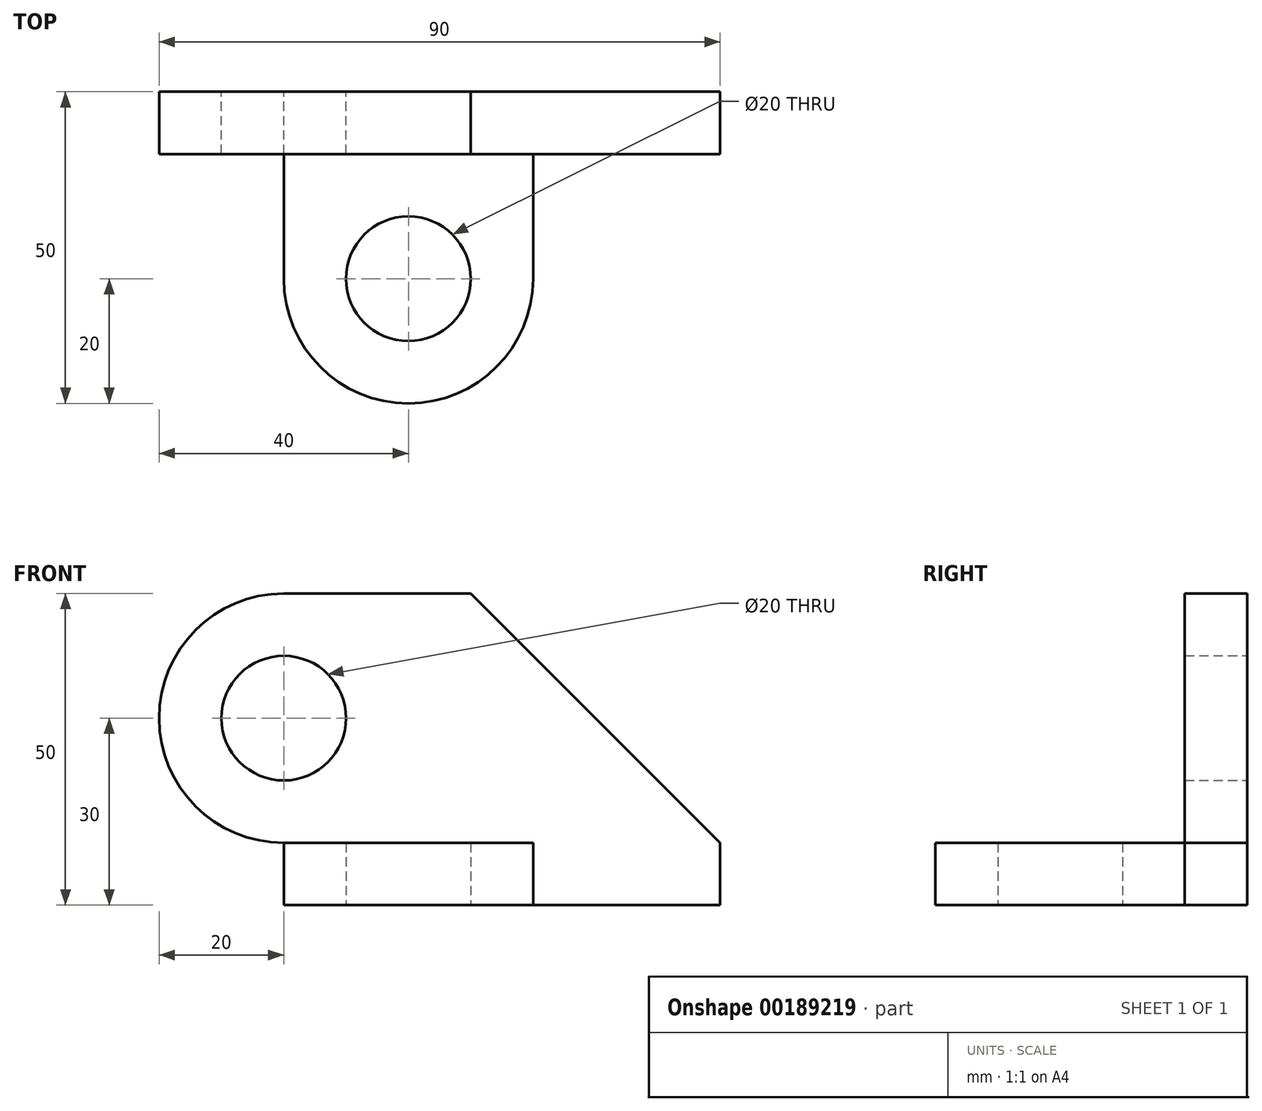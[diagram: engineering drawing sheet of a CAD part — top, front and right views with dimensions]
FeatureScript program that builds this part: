
annotation { "Feature Type Name" : "Feature", "Feature Type Description" : "" }
export const myFeature = defineFeature(function(context is Context, id is Id, definition is map)
    precondition{}
    {
        {
            var Q0;
            Q0=qCreatedBy(makeId("Top.planeOp"),FACE);
            var sketch = newSketch(context, id + "F0", { "sketchPlane" : qUnion([Q0])});
            skLineSegment(sketch, "E0.top", {"start": v(0, 30) * mm, "end": v(40, 30) * mm});
            skLineSegment(sketch, "E0.left", {"start": v(0, 0) * mm, "end": v(0, 30) * mm});
            skLineSegment(sketch, "E0.right", {"start": v(40, 0) * mm, "end": v(40, 30) * mm});
            skArc(sketch, "E1", {"start": v(0, 0) * mm, "mid": v(20, -20) * mm, "end": v(40, 0) * mm});
            skCircle(sketch, "E2", {"center": v(20, 0) * mm, "radius": 10 * mm});
            skSolve(sketch);
        }
        {
            var Q0;
            Q0=makeQuery(id+"F0.imprint","IMPRINT",FACE,{"disambiguationData":[TD([[makeQuery(id+"F0.imprint","IMPRINT",EDGE,{"derivedFrom":sQuery(id+"F0.wireOp",EDGE,"E0.top")}),-1.0]])]});
            extrude(context, id + "F1", {"entities" : qUnion([Q0]), "depth" : 10 * mm});
        }
        {
            var Q0;
            Q0=makeQuery(id+"F1.opExtrude","SWEPT_FACE",FACE,{"disambiguationData":[OSD([sQuery(id+"F0.wireOp",EDGE,"E0.top")])]});
            var sketch = newSketch(context, id + "F2", { "sketchPlane" : qUnion([Q0])});
            skLineSegment(sketch, "E3", {"start": v(-40, 0) * mm, "end": v(-70, 0) * mm});
            skLineSegment(sketch, "E4", {"start": v(-70, 0) * mm, "end": v(-70, 10) * mm});
            skLineSegment(sketch, "E5", {"start": v(-70, 10) * mm, "end": v(-30, 50) * mm});
            skLineSegment(sketch, "E6", {"start": v(-30, 50) * mm, "end": v(0, 50) * mm});
            skLineSegment(sketch, "E7.0", {"start": v(-40, 10) * mm, "end": v(0, 10) * mm});
            skLineSegment(sketch, "E8.0", {"start": v(-40, 10) * mm, "end": v(-40, 0) * mm});
            skArc(sketch, "E9", {"start": v(0, 10) * mm, "mid": v(20, 30) * mm, "end": v(0, 50) * mm});
            skCircle(sketch, "E10", {"center": v(0, 30) * mm, "radius": 10 * mm});
            skSolve(sketch);
        }
        {
            var Q0;
            Q0=makeQuery(id+"F2.imprint","IMPRINT",FACE,{"disambiguationData":[TD([[makeQuery(id+"F2.imprint","IMPRINT",EDGE,{"derivedFrom":sQuery(id+"F2.wireOp",EDGE,"E3")}),-1.0]])]});
            extrude(context, id + "F3", {"entities" : qUnion([Q0]), "operationType" : NewBodyOperationType.ADD, "oppositeDirection" : true, "depth" : 10 * mm});
        }
    });
